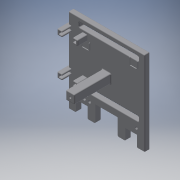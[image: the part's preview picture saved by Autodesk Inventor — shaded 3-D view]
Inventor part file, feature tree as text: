
AUTODESK INVENTOR PART (.ipt)
format: ipt  version: 2018 (Build 220112000, 112)  size: 1,007,616 bytes
history: native  units: in
note: dims shown in document units (in); Inventor stores cm internally (conversion verified against a paired STEP export)
features: reference x29, extrude x15, sketch x15, fillet x13, other x11, plane x7, projected_geometry x4
ambient origin geometry x8: Origin, YZ Plane, XZ Plane, XY Plane, X Axis, Y Axis, Z Axis, Center Point
bodies: Solid1 (feature_tree)
feature tree (94):
  extrude  "Extrusion1"  Depth=0.2839in
  sketch  "Sketch2"  dims[d6=0.2839in d7=2.1654in]
  plane  "Work Plane1"
  extrude  "Extrusion2"  Depth=2.1654in
  extrude  "Extrusion3"  Depth=0.1969in
  sketch  "Sketch4"  dims[d12=0.1969in d14=0.1181in d15=0.0in]
  plane  "Work Plane2"
  extrude  "Extrusion4"  Depth=0.1969in TaperAngle=0.0deg
  sketch  "Sketch5"  dims[d16=0.0098in d17=0.1969in]
  plane  "Work Plane3"
  extrude  "Extrusion5"  Depth=0.1969in
  sketch  "Sketch6"  dims[d18=1.0in d19=0.0in d20=0.1969in d21=0.0in]
  plane  "Work Plane4"
  extrude  "Extrusion6"  Depth=0.1969in TaperAngle=0.0deg
  sketch  "Sketch7"  dims[d22=0.0098in d23=2.0in]
  plane  "Work Plane5"
  extrude  "Extrusion7"  Depth=0.0098in
  sketch  "Sketch8"  dims[d24=0.1969in d25=0.0in d27=0.1969in d28=0.0098in d29=0.0098in d30=0.0692in d31=0.1181in d32=0.1969in d33=0.0in]
  plane  "Work Plane6"
  extrude  "Extrusion8"  Depth=0.1969in
  fillet  "Fillet1"  Radius=0.0098in
  fillet  "Fillet4"  Radius=0.0098in
  fillet  "Fillet5"  Radius=0.0692in
  fillet  "Fillet6"  Radius=0.1181in
  fillet  "Fillet7"  Radius=0.1969in
  extrude  "Extrusion9"  Depth=0.1969in TaperAngle=0.0deg
  extrude  "Extrusion10"  Depth=0.0098in
  fillet  "Fillet9"  Radius=0.1575in
  extrude  "Extrusion11"  Depth=0.0787in
  fillet  "Fillet10"  Radius=0.1969in
  fillet  "Fillet11"  Radius=0.0394in
  fillet  "Fillet12"  Radius=0.0394in
  extrude  "Extrusion12"  Depth=0.0394in
  fillet  "Fillet13"  Radius=0.0394in
  sketch  "Sketch13"  dims[d61=1.0in d62=0.5in d63=0.0in d64=0.0in d65=1.0in d66=0.0in]
  plane  "Work Plane7"
  extrude  "Extrusion13"  Depth=0.5in TaperAngle=0.0deg
  extrude  "Extrusion14"  Depth=0.0394in TaperAngle=0.0deg
  fillet  "Fillet14"  Radius=0.0394in
  fillet  "Fillet15"  Radius=0.0394in
  extrude  "Extrusion15"  Depth=0.0098in
  fillet  "Fillet16"  Radius=1.0197in
  sketch  "Sketch1"  dims[d3=1.0236in d5=0.2839in]
  reference  "Reference2"
  reference  "Reference3"
  sketch  "Sketch3"  dims[d8=0.1969in d9=0.1969in]
  projected_geometry  "Projected Loop1"
  reference  "Reference4"
  reference  "Reference5"
  reference  "Reference6"
  reference  "Reference7"
  reference  "Reference8"
  reference  "Reference9"
  reference  "Reference10"
  reference  "Reference11"
  reference  "Reference12"
  reference  "Reference13"
  reference  "Reference14"
  reference  "Reference15"
  reference  "Reference16"
  reference  "Reference17"
  reference  "Reference18"
  reference  "Reference19"
  reference  "Reference20"
  reference  "Reference21"
  sketch  "Sketch9"  dims[d34=0.1969in d35=0.0in d36=0.1969in d37=0.0in]
  sketch  "Sketch10"  dims[d43=0.0098in d44=0.0098in d45=0.1575in]
  projected_geometry  "Projected Loop2"
  projected_geometry  "Projected Loop3"
  sketch  "Sketch11"  dims[d46=0.0787in d48=0.0787in d52=0.1969in d53=0.0in d54=0.0394in d57=0.0394in]
  projected_geometry  "Projected Loop4"
  sketch  "Sketch12"  dims[d58=0.0394in d59=0.0394in d60=0.0394in]
  reference  "Reference22"
  sketch  "Sketch14"  dims[d68=0.0394in d69=0.1181in d70=0.0in d71=0.0394in d72=0.0394in]
  sketch  "Sketch15"  dims[d73=0.0394in d74=0.5098in d75=1.0197in d76=0.75in d77=0.2598in d78=0.5197in d79=0.5in d80=1.0in d81=0.0in d82=0.0394in d83=0.1969in d84=0.1969in d85=0.3937in d86=0.3937in d87=1.0in d88=0.0in d89=0.1083in d90=0.3937in d91=0.0in d92=0.0394in d93=0.0394in d94=0.0098in d95=0.0098in d96=0.0394in d97=0.0394in d98=0.0098in d99=0.0394in d100=0.0098in d108=0.0098in d109=0.0098in d110=0.0394in d111=0.0394in d112=0.0098in d113=0.0394in d114=0.0098in d115=0.0098in d116=0.0098in d117=0.0098in d118=0.0394in d119=0.0in d120=0.0098in]
  reference  "Reference23"
  reference  "Reference24"
  reference  "Reference25"
  reference  "Reference26"
  reference  "Reference27"
  reference  "Reference28"
  reference  "Reference29"
  reference  "Reference30"
  other  "<userpath>\OneDrive\Documents\Inventor\TSA\2018\Animatronics\Tortoise\TurtleAssembly2.iam"
  other  "TurtleAssembly2.iam"
  other  "arduino uno:3"
  other  "PCB_Final_Default:1"
  other  "HeadOpenRack:3"
  other  "servo (2):9"
  other  "Frame - Copy:1"
  other  "SyringeAttachment:7"
  other  "Tail_Servo_Mount:1"
  other  "TableLeg:5"
  other  "TableLeg:4"
